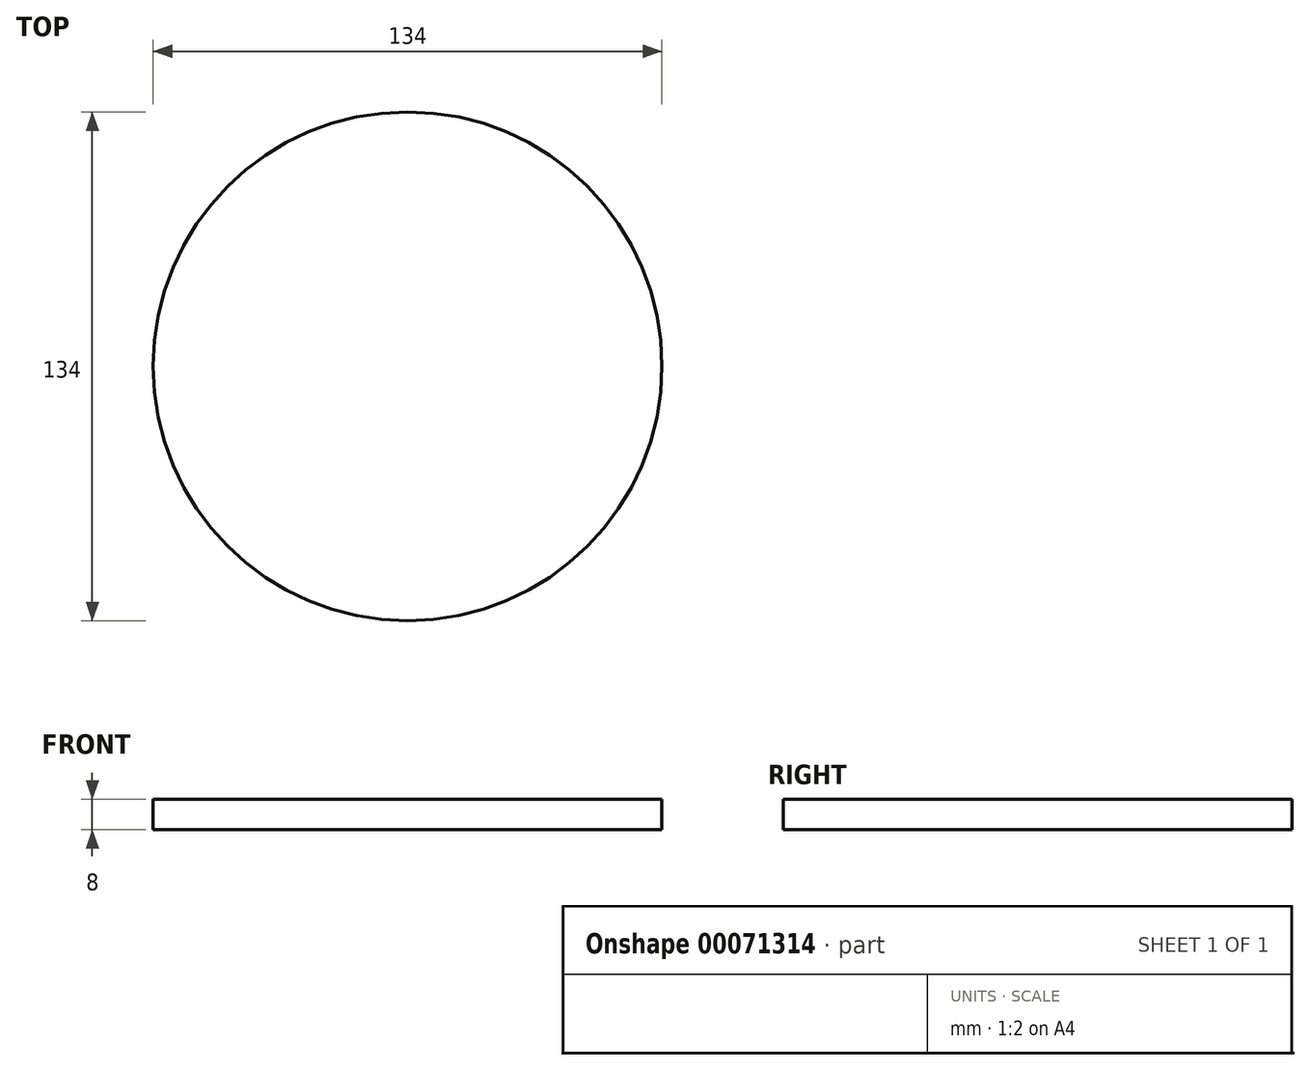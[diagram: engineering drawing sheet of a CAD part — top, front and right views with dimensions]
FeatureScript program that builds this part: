
annotation { "Feature Type Name" : "Feature", "Feature Type Description" : "" }
export const myFeature = defineFeature(function(context is Context, id is Id, definition is map)
    precondition{}
    {
        {
            var Q0;
            Q0=qCreatedBy(makeId("Top.planeOp"),FACE);
            var sketch = newSketch(context, id + "F0", { "sketchPlane" : qUnion([Q0])});
            skCircle(sketch, "E0", {"center": v(0, 0) * mm, "radius": 67 * mm});
            skSolve(sketch);
        }
        {
            var Q0;
            Q0=makeQuery(id+"F0.imprint","IMPRINT",FACE,{"disambiguationData":[TD([[makeQuery(id+"F0.imprint","IMPRINT",EDGE,{"derivedFrom":sQuery(id+"F0.wireOp",EDGE,"E0")}),1.0]])]});
            extrude(context, id + "F1", {"entities" : qUnion([Q0]), "endBound" : BoundingType.SYMMETRIC, "depth" : 5 * mm});
        }
        {
            var Q0;
            Q0=makeQuery(id+"F1.opExtrude","CAP_FACE",FACE,{"disambiguationData":[OSD([sQuery(id+"F0.wireOp",EDGE,"E0")])],"isStart":false});
            var sketch = newSketch(context, id + "F2", { "sketchPlane" : qUnion([Q0])});
            skCircle(sketch, "E1", {"center": v(0, 0) * mm, "radius": 64.38 * mm});
            skCircle(sketch, "E2", {"center": v(0, 0) * mm, "radius": 62.62 * mm});
            skCircle(sketch, "E3", {"center": v(0, 0) * mm, "radius": 58.88 * mm});
            skSolve(sketch);
        }
        {
            var Q0;
            Q0=makeQuery(id+"F2.imprint","IMPRINT",FACE,{"disambiguationData":[TD([[makeQuery(id+"F2.imprint","IMPRINT",EDGE,{"derivedFrom":sQuery(id+"F2.wireOp",EDGE,"E1")}),1.0]])]});
            var Q1;
            Q1=makeQuery(id+"F1.opExtrude","CAP_FACE",FACE,{"disambiguationData":[OSD([sQuery(id+"F0.wireOp",EDGE,"E0")])],"isStart":true});
            extrude(context, id + "F3", {"entities" : qUnion([Q0, Q1]), "operationType" : NewBodyOperationType.ADD, "oppositeDirection" : true, "depth" : 3 * mm});
        }
    });
